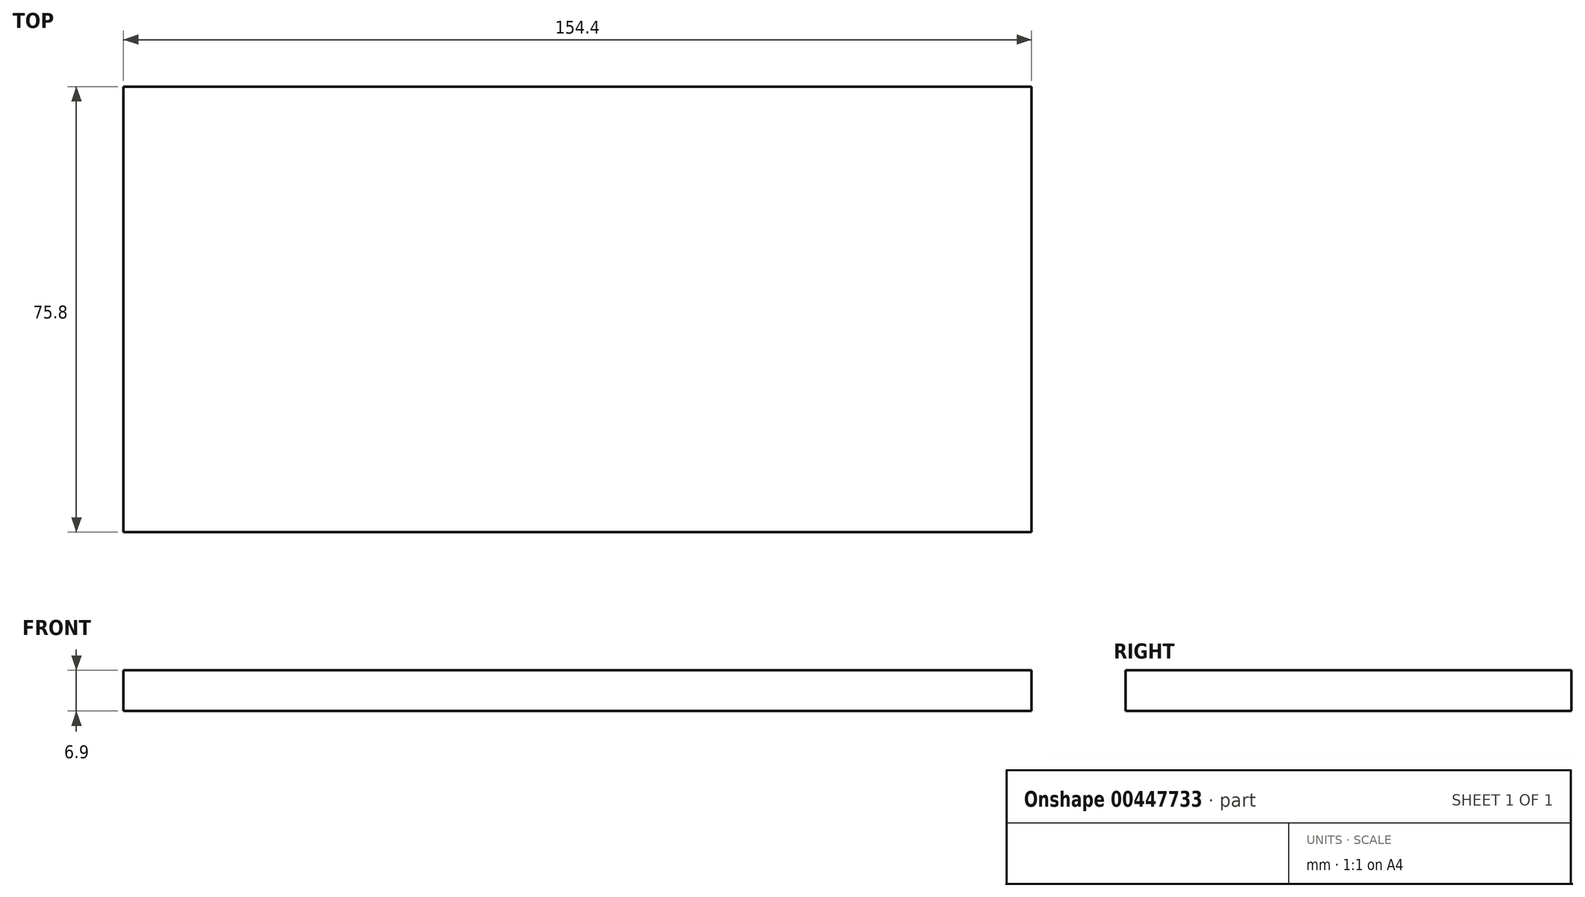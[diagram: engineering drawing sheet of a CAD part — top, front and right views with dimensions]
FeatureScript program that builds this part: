
annotation { "Feature Type Name" : "Feature", "Feature Type Description" : "" }
export const myFeature = defineFeature(function(context is Context, id is Id, definition is map)
    precondition{}
    {
        {
            var Q0;
            Q0=qCreatedBy(makeId("Top.planeOp"),FACE);
            var sketch = newSketch(context, id + "F0", { "sketchPlane" : qUnion([Q0])});
            skLineSegment(sketch, "E0.bottom", {"start": v(-75.61, 34.33) * mm, "end": v(78.79, 34.33) * mm});
            skLineSegment(sketch, "E0.top", {"start": v(-75.61, -41.47) * mm, "end": v(78.79, -41.47) * mm});
            skLineSegment(sketch, "E0.left", {"start": v(-75.61, 34.33) * mm, "end": v(-75.61, -41.47) * mm});
            skLineSegment(sketch, "E0.right", {"start": v(78.79, 34.33) * mm, "end": v(78.79, -41.47) * mm});
            skSolve(sketch);
        }
        {
            var Q0;
            Q0 = qSketchRegion(id + "F0", true);
            extrude(context, id + "F1", {"entities" : qUnion([Q0]), "depth" : 6.9 * mm});
        }
    });
